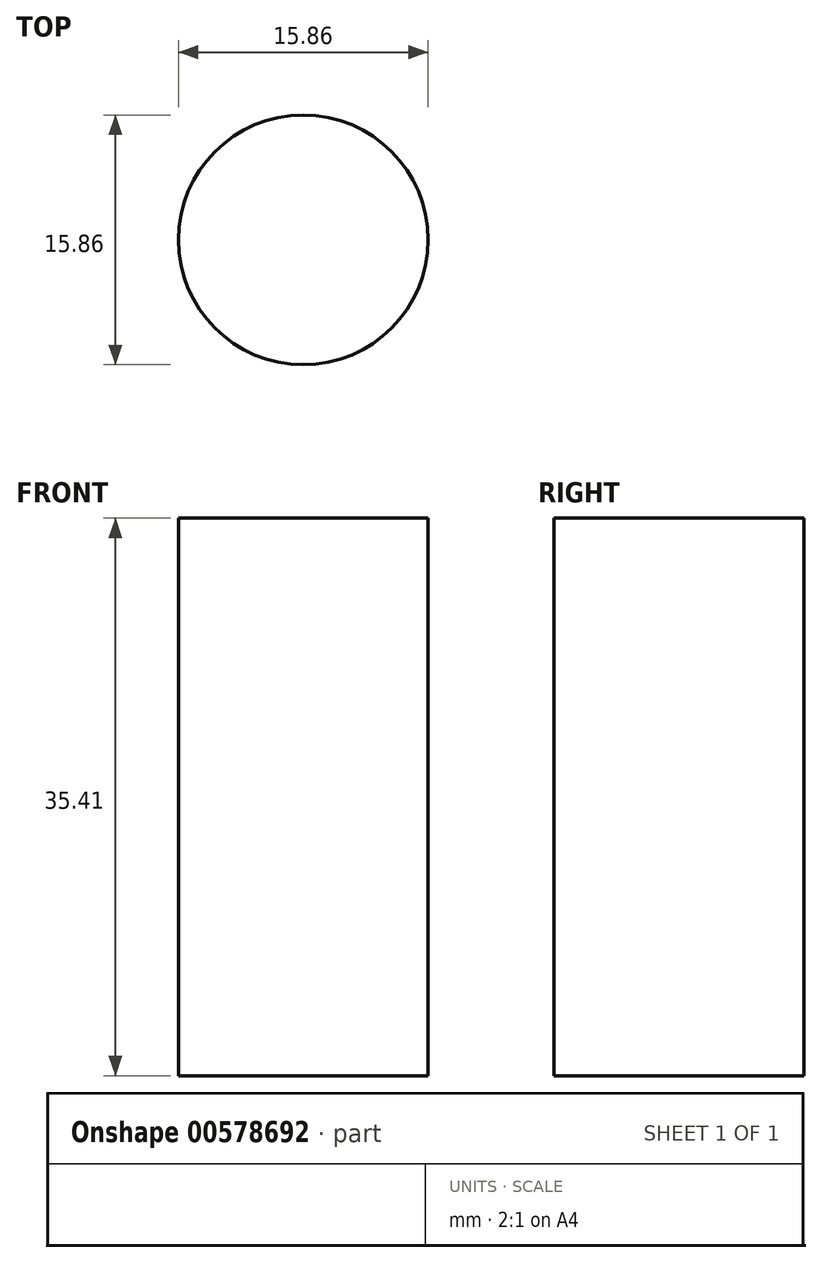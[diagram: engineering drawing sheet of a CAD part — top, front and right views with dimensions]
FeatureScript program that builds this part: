
annotation { "Feature Type Name" : "Feature", "Feature Type Description" : "" }
export const myFeature = defineFeature(function(context is Context, id is Id, definition is map)
    precondition{}
    {
        {
            var Q0;
            Q0=qCreatedBy(makeId("Top.planeOp"),FACE);
            var sketch = newSketch(context, id + "F0", { "sketchPlane" : qUnion([Q0])});
            skCircle(sketch, "E0", {"center": v(0, 0) * mm, "radius": 7.93 * mm});
            skSolve(sketch);
        }
        {
            var Q0;
            Q0 = qSketchRegion(id + "F0", true);
            extrude(context, id + "F1", {"entities" : qUnion([Q0]), "depth" : 35.4 * mm, "offsetDistance" : 25.4 * mm});
        }
    });
